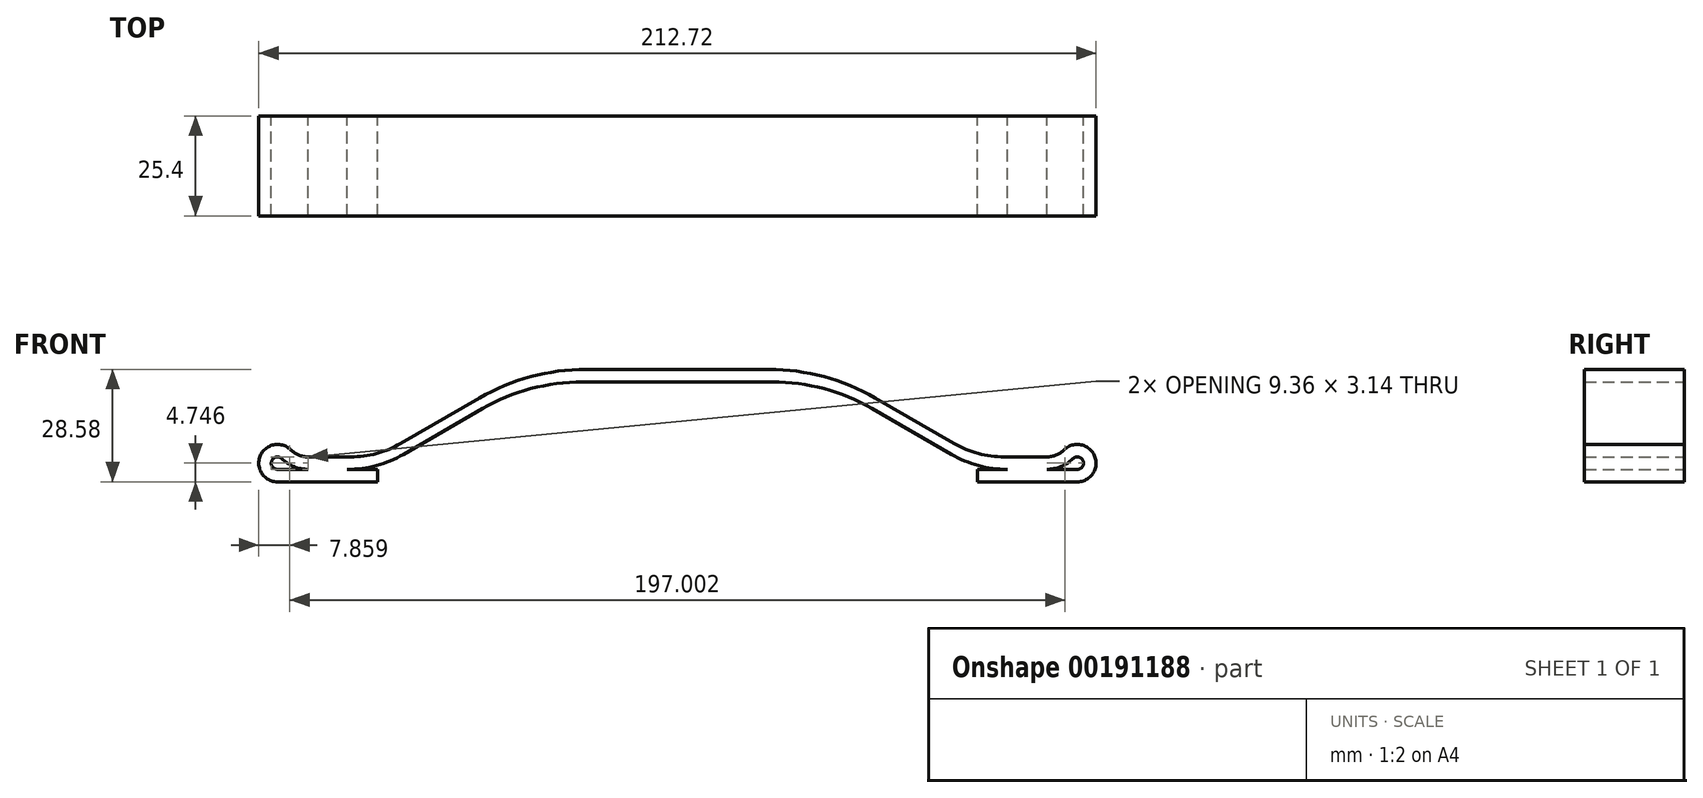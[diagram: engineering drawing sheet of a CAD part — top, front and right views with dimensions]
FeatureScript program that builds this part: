
annotation { "Feature Type Name" : "Feature", "Feature Type Description" : "" }
export const myFeature = defineFeature(function(context is Context, id is Id, definition is map)
    precondition{}
    {
        {
            var Q0;
            Q0=qCreatedBy(makeId("Front.planeOp"),FACE);
            var sketch = newSketch(context, id + "F0", { "sketchPlane" : qUnion([Q0])});
            skLineSegment(sketch, "E0.bottom", {"start": v(-76.2, 0) * mm, "end": v(-101.6, 0) * mm});
            skLineSegment(sketch, "E0.top", {"start": v(-76.2, 3.17) * mm, "end": v(-101.6, 3.17) * mm});
            skLineSegment(sketch, "E0.left", {"start": v(-76.2, 0) * mm, "end": v(-76.2, 3.17) * mm});
            skLineSegment(sketch, "E1.top", {"start": v(-93.82, 6.35) * mm, "end": v(-83, 6.35) * mm});
            skLineSegment(sketch, "E2", {"start": v(-24.1, 25.4) * mm, "end": v(0, 25.4) * mm});
            skLineSegment(sketch, "E3", {"start": v(0, 25.4) * mm, "end": v(0, 28.58) * mm});
            skLineSegment(sketch, "E4", {"start": v(0, 28.58) * mm, "end": v(-23.24, 28.57) * mm});
            skLineSegment(sketch, "E5", {"start": v(-69.57, 7) * mm, "end": v(-49.5, 18.6) * mm});
            skLineSegment(sketch, "E6", {"start": v(-70.3, 9.75) * mm, "end": v(-50.23, 21.34) * mm});
            skArc(sketch, "E7.filletArc", {"start": v(-24.1, 25.4) * mm, "mid": v(-37.24, 23.67) * mm, "end": v(-49.5, 18.6) * mm});
            skArc(sketch, "E8.filletArc", {"start": v(-83, 6.35) * mm, "mid": v(-76.43, 7.22) * mm, "end": v(-70.3, 9.75) * mm});
            skPoint(sketch, "E9.visualSharp", {"position": v(-76.2, 3.17) * mm});
            skArc(sketch, "E9.filletArc", {"start": v(-83.86, 3.17) * mm, "mid": v(-76.46, 4.15) * mm, "end": v(-69.57, 7) * mm});
            skArc(sketch, "E10.filletArc", {"start": v(-23.24, 28.58) * mm, "mid": v(-37.21, 26.74) * mm, "end": v(-50.23, 21.34) * mm});
            skArc(sketch, "E11", {"start": v(-98.27, 8.16) * mm, "mid": v(-106, 6.56) * mm, "end": v(-101.6, 0) * mm});
            skPoint(sketch, "E12.visualSharp", {"position": v(-97.1, 6.35) * mm});
            skArc(sketch, "E12.filletArc", {"start": v(-98.27, 8.16) * mm, "mid": v(-96.22, 6.82) * mm, "end": v(-93.82, 6.35) * mm});
            skPoint(sketch, "E13.visualSharp", {"position": v(-101.6, 0) * mm});
            skArc(sketch, "E14", {"start": v(-100.49, 5.9) * mm, "mid": v(-103.07, 5.36) * mm, "end": v(-101.6, 3.17) * mm});
            skArc(sketch, "E15.filletArc", {"start": v(-100.49, 5.9) * mm, "mid": v(-97.42, 3.88) * mm, "end": v(-93.82, 3.17) * mm});
            skLineSegment(sketch, "E16.MirrorCS", {"start": v(0, 28.58) * mm, "end": v(23.24, 28.57) * mm});
            skLineSegment(sketch, "E17.MirrorCS", {"start": v(24.1, 25.4) * mm, "end": v(0, 25.4) * mm});
            skArc(sketch, "E18.MirrorCS", {"start": v(24.1, 25.4) * mm, "mid": v(37.24, 23.67) * mm, "end": v(49.5, 18.6) * mm});
            skArc(sketch, "E19.MirrorCS", {"start": v(23.24, 28.58) * mm, "mid": v(37.21, 26.74) * mm, "end": v(50.23, 21.34) * mm});
            skLineSegment(sketch, "E20.MirrorCS", {"start": v(70.3, 9.75) * mm, "end": v(50.23, 21.34) * mm});
            skLineSegment(sketch, "E21.MirrorCS", {"start": v(69.57, 7) * mm, "end": v(49.5, 18.6) * mm});
            skArc(sketch, "E22.MirrorCS", {"start": v(83.86, 3.17) * mm, "mid": v(76.46, 4.15) * mm, "end": v(69.57, 7) * mm});
            skArc(sketch, "E23.MirrorCS", {"start": v(83, 6.35) * mm, "mid": v(76.43, 7.22) * mm, "end": v(70.3, 9.75) * mm});
            skLineSegment(sketch, "E24.MirrorCS", {"start": v(93.82, 6.35) * mm, "end": v(83, 6.35) * mm});
            skLineSegment(sketch, "E25.MirrorCS", {"start": v(76.2, 3.17) * mm, "end": v(101.6, 3.17) * mm});
            skArc(sketch, "E26.MirrorCS", {"start": v(98.27, 8.16) * mm, "mid": v(96.22, 6.82) * mm, "end": v(93.82, 6.35) * mm});
            skArc(sketch, "E27.MirrorCS", {"start": v(98.27, 8.16) * mm, "mid": v(106, 6.56) * mm, "end": v(101.6, 0) * mm});
            skArc(sketch, "E28.MirrorCS", {"start": v(100.49, 5.9) * mm, "mid": v(97.42, 3.88) * mm, "end": v(93.82, 3.17) * mm});
            skArc(sketch, "E29.MirrorCS", {"start": v(100.49, 5.9) * mm, "mid": v(103.07, 5.36) * mm, "end": v(101.6, 3.17) * mm});
            skLineSegment(sketch, "E30.MirrorCS", {"start": v(76.2, 0) * mm, "end": v(101.6, 0) * mm});
            skLineSegment(sketch, "E31.MirrorCS", {"start": v(76.2, 0) * mm, "end": v(76.2, 3.17) * mm});
            skSolve(sketch);
        }
        {
            var Q0;
            Q0 = qSketchRegion(id + "F0", true);
            extrude(context, id + "F1", {"entities" : qUnion([Q0]), "depth" : 25.4 * mm});
        }
    });
